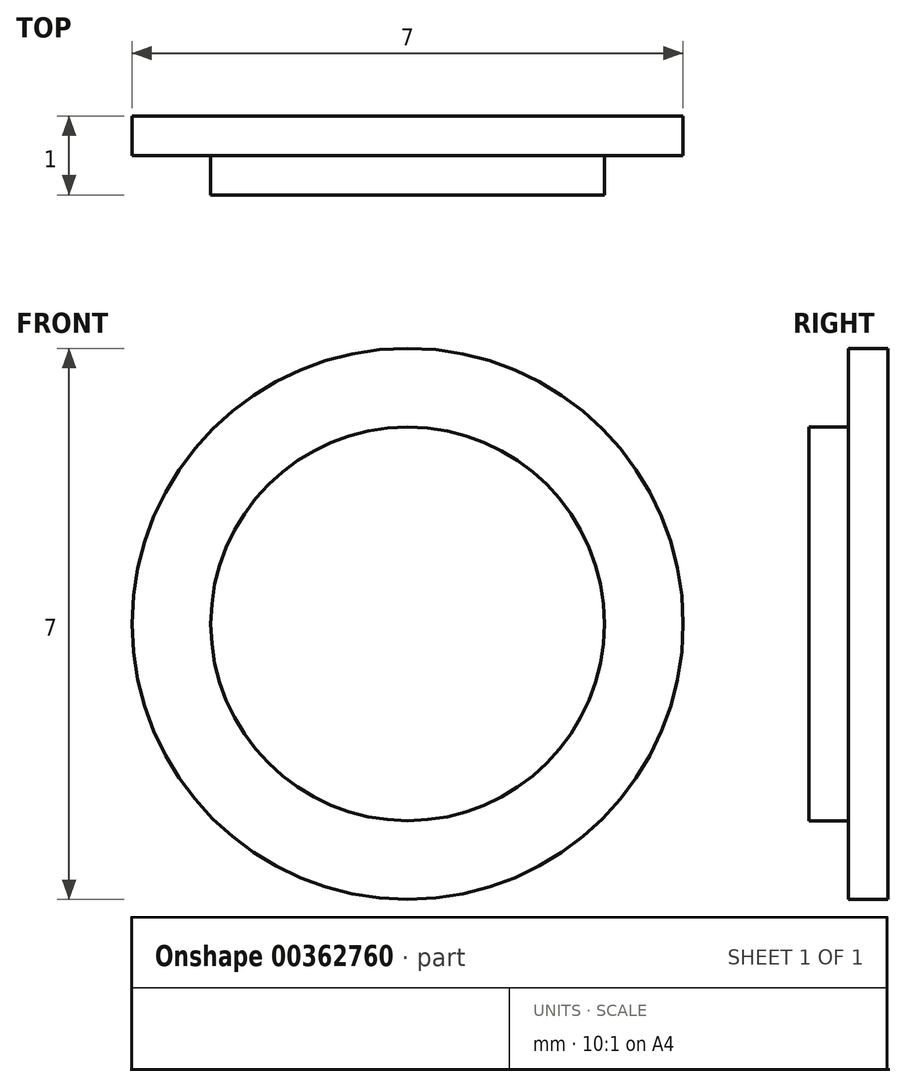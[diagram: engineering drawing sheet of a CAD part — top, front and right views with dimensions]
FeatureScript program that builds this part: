
annotation { "Feature Type Name" : "Feature", "Feature Type Description" : "" }
export const myFeature = defineFeature(function(context is Context, id is Id, definition is map)
    precondition{}
    {
        {
            var Q0;
            Q0=qCreatedBy(makeId("Front.planeOp"),FACE);
            var sketch = newSketch(context, id + "F0", { "sketchPlane" : qUnion([Q0])});
            skCircle(sketch, "E0", {"center": v(0, 0) * mm, "radius": 2.5 * mm});
            skCircle(sketch, "E1", {"center": v(0, 0) * mm, "radius": 3.5 * mm});
            skSolve(sketch);
        }
        {
            var Q0;
            Q0=makeQuery(id+"F0.imprint","IMPRINT",FACE,{"disambiguationData":[TD([[makeQuery(id+"F0.imprint","IMPRINT",EDGE,{"derivedFrom":sQuery(id+"F0.wireOp",EDGE,"E0")}),1.0]])]});
            extrude(context, id + "F1", {"entities" : qUnion([Q0]), "depth" : 1 * mm});
        }
        {
            var Q0;
            Q0=qCreatedBy(makeId("Front.planeOp"),FACE);
            var sketch = newSketch(context, id + "F2", { "sketchPlane" : qUnion([Q0])});
            skCircle(sketch, "E2", {"center": v(0, 0) * mm, "radius": 3.5 * mm});
            skSolve(sketch);
        }
        {
            var Q0;
            Q0 = qSketchRegion(id + "F2", true);
            extrude(context, id + "F3", {"entities" : qUnion([Q0]), "operationType" : NewBodyOperationType.ADD, "depth" : 0.5 * mm});
        }
    });
